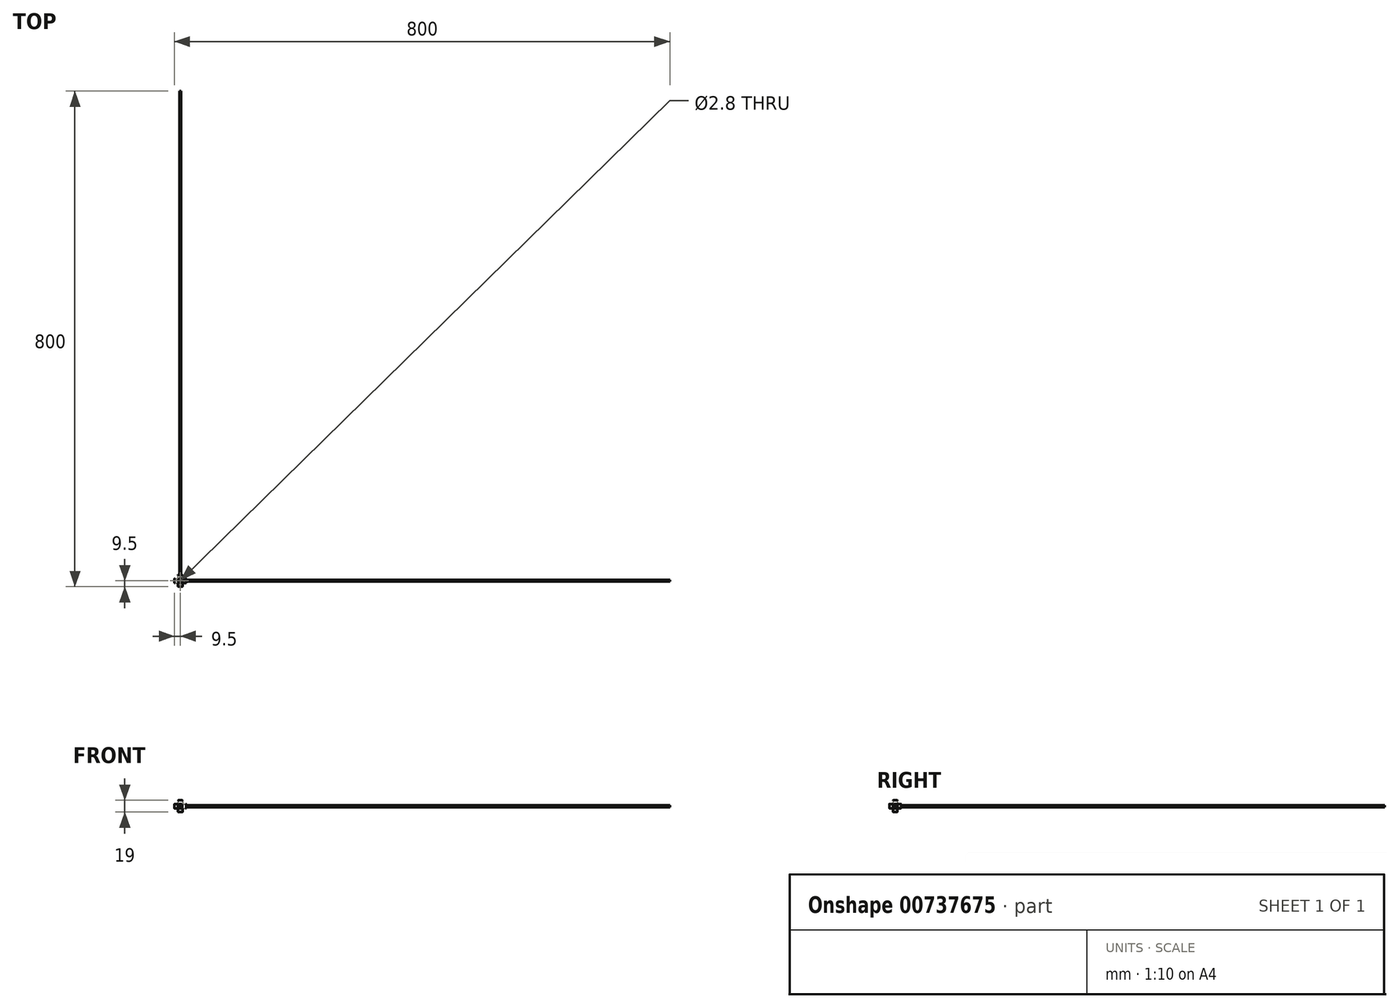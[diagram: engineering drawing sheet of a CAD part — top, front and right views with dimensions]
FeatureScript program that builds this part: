
annotation { "Feature Type Name" : "Feature", "Feature Type Description" : "" }
export const myFeature = defineFeature(function(context is Context, id is Id, definition is map)
    precondition{}
    {
        {
            var Q0;
            Q0=qCreatedBy(makeId("Front.planeOp"),FACE);
            var sketch = newSketch(context, id + "F0", { "sketchPlane" : qUnion([Q0])});
            skCircle(sketch, "E0", {"center": v(0, 0) * mm, "radius": 3.55 * mm});
            skSolve(sketch);
        }
        {
            var Q0;
            Q0 = qSketchRegion(id + "F0", true);
            extrude(context, id + "F1", {"entities" : qUnion([Q0]), "endBound" : BoundingType.SYMMETRIC, "depth" : 19 * mm, "offsetDistance" : 25 * mm});
        }
        {
            var Q0;
            Q0=qCreatedBy(makeId("Front.planeOp"),FACE);
            var sketch = newSketch(context, id + "F2", { "sketchPlane" : qUnion([Q0])});
            skLineSegment(sketch, "E1.bottom", {"start": v(0, 0) * mm, "end": v(0, 0) * mm});
            skLineSegment(sketch, "E1.top", {"start": v(0, 0) * mm, "end": v(0, 0) * mm});
            skLineSegment(sketch, "E1.left", {"start": v(0, 0) * mm, "end": v(0, 0) * mm});
            skLineSegment(sketch, "E1.right", {"start": v(0, 0) * mm, "end": v(0, 0) * mm});
            skLineSegment(sketch, "E2.bottom", {"start": v(0, 0) * mm, "end": v(-10, 0) * mm});
            skLineSegment(sketch, "E2.top", {"start": v(0, 10) * mm, "end": v(-10, 10) * mm});
            skLineSegment(sketch, "E2.left", {"start": v(0, 0) * mm, "end": v(0, 10) * mm});
            skLineSegment(sketch, "E2.right", {"start": v(-10, 0) * mm, "end": v(-10, 10) * mm});
            skSolve(sketch);
        }
        {
            var Q0;
            Q0=makeQuery(id+"F2.imprint","IMPRINT",FACE,{"disambiguationData":[TD([[makeQuery(id+"F2.imprint","IMPRINT",EDGE,{"derivedFrom":sQuery(id+"F2.wireOp",EDGE,"E2.bottom")}),-1.0]])]});
            extrude(context, id + "F3", {"entities" : qUnion([Q0]), "depth" : 10 * mm, "offsetDistance" : 25 * mm});
        }
        {
            var Q0;
            Q0=makeQuery(id+"F3.opExtrude","CAP_VERTEX",VERTEX,{"disambiguationData":[OSD([sQuery(id+"F2.wireOp",EDGE,"E2.bottom"),sQuery(id+"F2.wireOp",EDGE,"E2.right")])],"isStart":true});
            var Q1;
            Q1=makeQuery(id+"F3.opExtrude","CAP_VERTEX",VERTEX,{"disambiguationData":[OSD([sQuery(id+"F2.wireOp",EDGE,"E2.top"),sQuery(id+"F2.wireOp",EDGE,"E2.right")])],"isStart":false});
            var Q2;
            Q2=makeQuery(id+"F3.opExtrude","CAP_VERTEX",VERTEX,{"disambiguationData":[OSD([sQuery(id+"F2.wireOp",EDGE,"E2.top"),sQuery(id+"F2.wireOp",EDGE,"E2.left")])],"isStart":false});
            cPlane(context, id + "F4", {"entities" : qUnion([Q0, Q1, Q2]), "cplaneType" : CPlaneType.THREE_POINT, "offset" : 25 * mm, "width" : 150 * mm, "height" : 150 * mm});
        }
        {
            var Q0;
            Q0=qCreatedBy(id+"F4.planeOp",FACE);
            var sketch = newSketch(context, id + "F5", { "sketchPlane" : qUnion([Q0])});
            skLineSegment(sketch, "E3", {"start": v(0, 0) * mm, "end": v(-10, 14.14) * mm});
            skSolve(sketch);
        }
        {
            var Q0;
            Q0=makeQuery(id+"F1.opExtrude","SWEPT_BODY",BODY,{"disambiguationData":[OSD([sQuery(id+"F0.wireOp",EDGE,"E0")])]});
            var Q1;
            Q1=sQuery(id+"F5.wireOp",EDGE,"E3");
            circularPattern(context, id + "F6", {"entities" : qUnion([Q0]), "axis" : qUnion([Q1]), "angle" : 360 * degree, "instanceCount" : 3, "equalSpace" : true});
        }
        {
            var Q0;
            Q0=makeQuery(id+"F3.opExtrude","SWEPT_BODY",BODY,{"disambiguationData":[OSD([sQuery(id+"F2.wireOp",EDGE,"E2.bottom"),sQuery(id+"F2.wireOp",EDGE,"E2.top"),sQuery(id+"F2.wireOp",EDGE,"E2.left"),sQuery(id+"F2.wireOp",EDGE,"E2.right")])]});
            deleteBodies(context, id + "F7", {"entities" : qUnion([Q0])});
        }
        {
            var Q0;
            Q0=makeQuery(id+"F1.opExtrude","CAP_FACE",FACE,{"disambiguationData":[OSD([sQuery(id+"F0.wireOp",EDGE,"E0")])],"isStart":false});
            var sketch = newSketch(context, id + "F8", { "sketchPlane" : qUnion([Q0])});
            skCircle(sketch, "E4", {"center": v(0, 0) * mm, "radius": 1.4 * mm});
            skSolve(sketch);
        }
        {
            var Q0;
            Q0 = qSketchRegion(id + "F8", true);
            extrude(context, id + "F9", {"entities" : qUnion([Q0]), "oppositeDirection" : true, "depth" : 800 * mm, "offsetDistance" : 25 * mm});
        }
        {
            var Q0;
            Q0=makeQuery(id+"F9.opExtrude","SWEPT_BODY",BODY,{"disambiguationData":[OSD([sQuery(id+"F8.wireOp",EDGE,"E4")])]});
            var Q1;
            Q1=sQuery(id+"F5.wireOp",EDGE,"E3");
            circularPattern(context, id + "F10", {"entities" : qUnion([Q0]), "axis" : qUnion([Q1]), "angle" : 360 * degree, "instanceCount" : 3, "equalSpace" : true});
        }
        {
            var Q0;
            Q0=makeQuery(id+"F10.opPattern","COPY",BODY,{"derivedFrom":makeQuery(id+"F9.opExtrude","SWEPT_BODY",BODY,{"disambiguationData":[OSD([sQuery(id+"F8.wireOp",EDGE,"E4")])]}),"instanceName":"1"});
            var Q1;
            Q1=makeQuery(id+"F1.opExtrude","SWEPT_BODY",BODY,{"disambiguationData":[OSD([sQuery(id+"F0.wireOp",EDGE,"E0")])]});
            booleanBodies(context, id + "F11", {"operationType" : BooleanOperationType.SUBTRACTION, "tools" : qUnion([Q0]), "targets" : qUnion([Q1])});
        }
        {
            var Q0;
            Q0=makeQuery(id+"F6.opPattern","COPY",FACE,{"derivedFrom":makeQuery(id+"F1.opExtrude","CAP_FACE",FACE,{"disambiguationData":[OSD([sQuery(id+"F0.wireOp",EDGE,"E0")])],"isStart":false}),"instanceName":"2"});
            var Q1;
            Q1=makeQuery(id+"F6.opPattern","COPY",FACE,{"derivedFrom":makeQuery(id+"F1.opExtrude","CAP_FACE",FACE,{"disambiguationData":[OSD([sQuery(id+"F0.wireOp",EDGE,"E0")])],"isStart":false}),"instanceName":"1"});
            var Q2;
            Q2=makeQuery(id+"F6.opPattern","COPY",FACE,{"derivedFrom":makeQuery(id+"F1.opExtrude","CAP_FACE",FACE,{"disambiguationData":[OSD([sQuery(id+"F0.wireOp",EDGE,"E0")])],"isStart":true}),"instanceName":"2"});
            var Q3;
            Q3=makeQuery(id+"F6.opPattern","COPY",FACE,{"derivedFrom":makeQuery(id+"F1.opExtrude","CAP_FACE",FACE,{"disambiguationData":[OSD([sQuery(id+"F0.wireOp",EDGE,"E0")])],"isStart":true}),"instanceName":"1"});
            var Q4;
            Q4=makeQuery(id+"F1.opExtrude","CAP_FACE",FACE,{"disambiguationData":[OSD([sQuery(id+"F0.wireOp",EDGE,"E0")])],"isStart":true});
            var Q5;
            Q5=makeQuery(id+"F1.opExtrude","CAP_FACE",FACE,{"disambiguationData":[OSD([sQuery(id+"F0.wireOp",EDGE,"E0")])],"isStart":false});
            fillet(context, id + "F12", {"entities" : qUnion([Q0, Q1, Q2, Q3, Q4, Q5]), "radius" : 0.5 * mm, "tangentPropagation" : true, "allowEdgeOverflow" : false});
        }
    });
